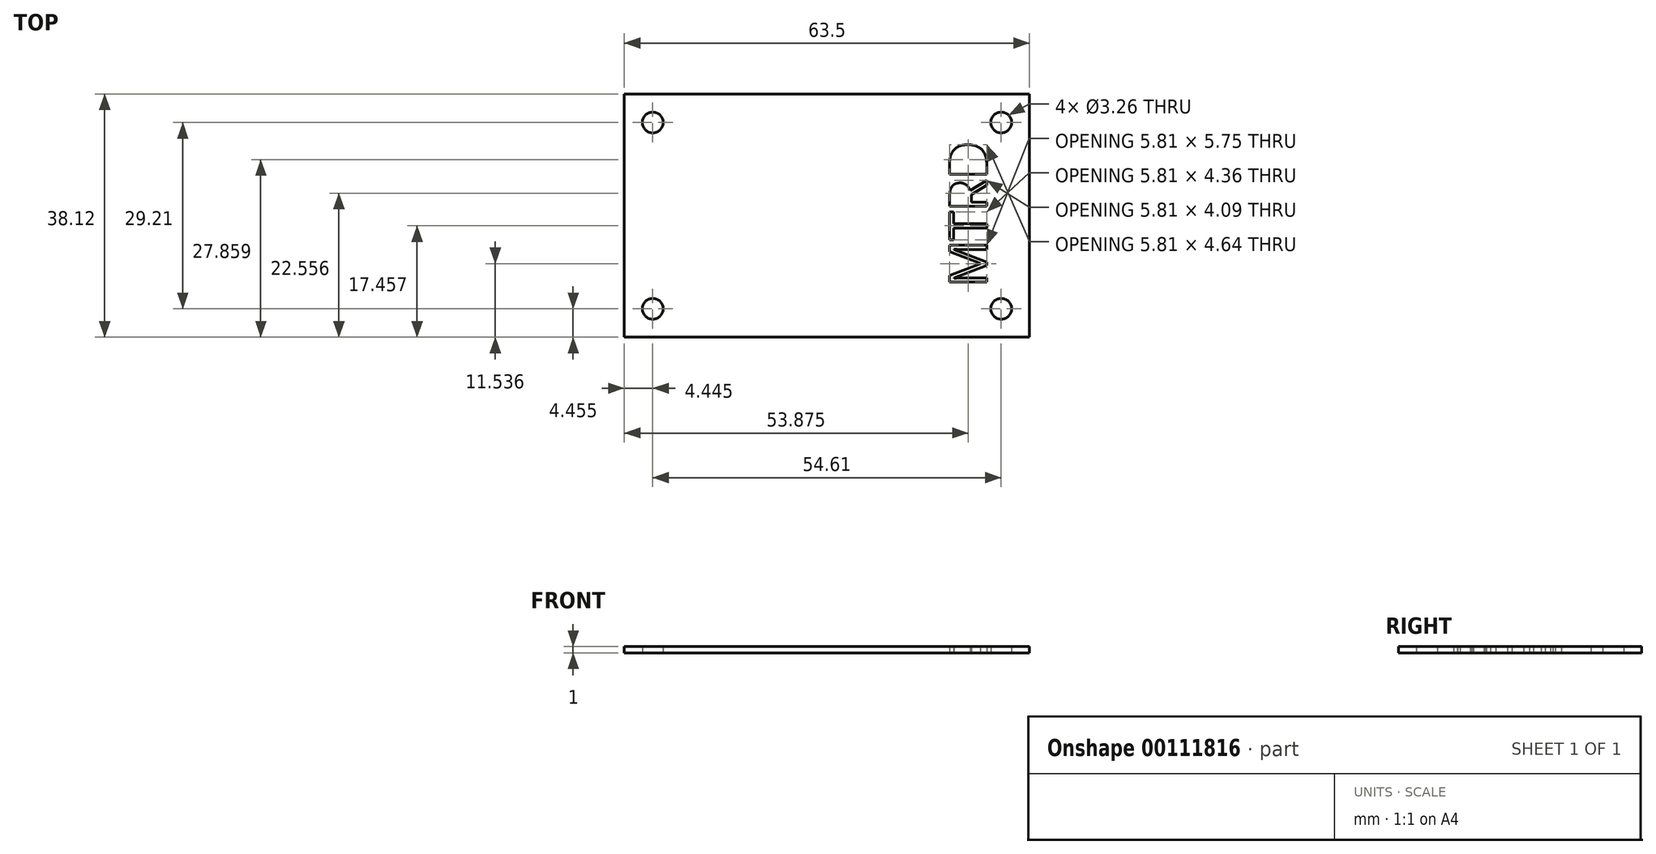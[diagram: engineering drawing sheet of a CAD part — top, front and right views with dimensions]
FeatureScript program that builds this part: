
annotation { "Feature Type Name" : "Feature", "Feature Type Description" : "" }
export const myFeature = defineFeature(function(context is Context, id is Id, definition is map)
    precondition{}
    {
        {
            var Q0;
            Q0=qCreatedBy(makeId("Top.planeOp"),FACE);
            var sketch = newSketch(context, id + "F0", { "sketchPlane" : qUnion([Q0])});
            skLineSegment(sketch, "E0.bottom", {"start": v(31.75, -19.05) * mm, "end": v(-31.75, -19.05) * mm});
            skLineSegment(sketch, "E0.top", {"start": v(31.75, 19.05) * mm, "end": v(-31.75, 19.05) * mm});
            skLineSegment(sketch, "E0.left", {"start": v(31.75, -19.05) * mm, "end": v(31.75, 19.06) * mm});
            skLineSegment(sketch, "E0.right", {"start": v(-31.75, -19.05) * mm, "end": v(-31.75, 19.05) * mm});
            skPoint(sketch, "E0.middle", {"position": v(0, 0) * mm});
            skLineSegment(sketch, "E1.bottom", {"start": v(27.3, -14.6) * mm, "end": v(-27.3, -14.6) * mm, "construction": true});
            skLineSegment(sketch, "E1.top", {"start": v(27.3, 14.6) * mm, "end": v(-27.3, 14.6) * mm, "construction": true});
            skLineSegment(sketch, "E1.left", {"start": v(27.3, -14.6) * mm, "end": v(27.3, 14.6) * mm, "construction": true});
            skLineSegment(sketch, "E1.right", {"start": v(-27.3, -14.6) * mm, "end": v(-27.3, 14.6) * mm, "construction": true});
            skCircle(sketch, "E2", {"center": v(-27.3, 14.6) * mm, "radius": 1.63 * mm});
            skCircle(sketch, "E3", {"center": v(27.3, 14.6) * mm, "radius": 1.63 * mm});
            skCircle(sketch, "E4", {"center": v(27.3, -14.6) * mm, "radius": 1.63 * mm});
            skCircle(sketch, "E5", {"center": v(-27.3, -14.6) * mm, "radius": 1.63 * mm});
            skText(sketch, "E6", { "text": "MTRD", "fontName": "OpenSans-Regular.ttf"});
            const initialGuessF0  = {"E6": [0.02503, -0.0112, 0, 1, 0.00586]};
            skSetInitialGuess(sketch, initialGuessF0);
            skSolve(sketch);
        }
        {
            var Q0;
            Q0 = qSketchRegion(id + "F0", true);
            extrude(context, id + "F1", {"entities" : qUnion([Q0]), "depth" : 1 * mm});
        }
    });
